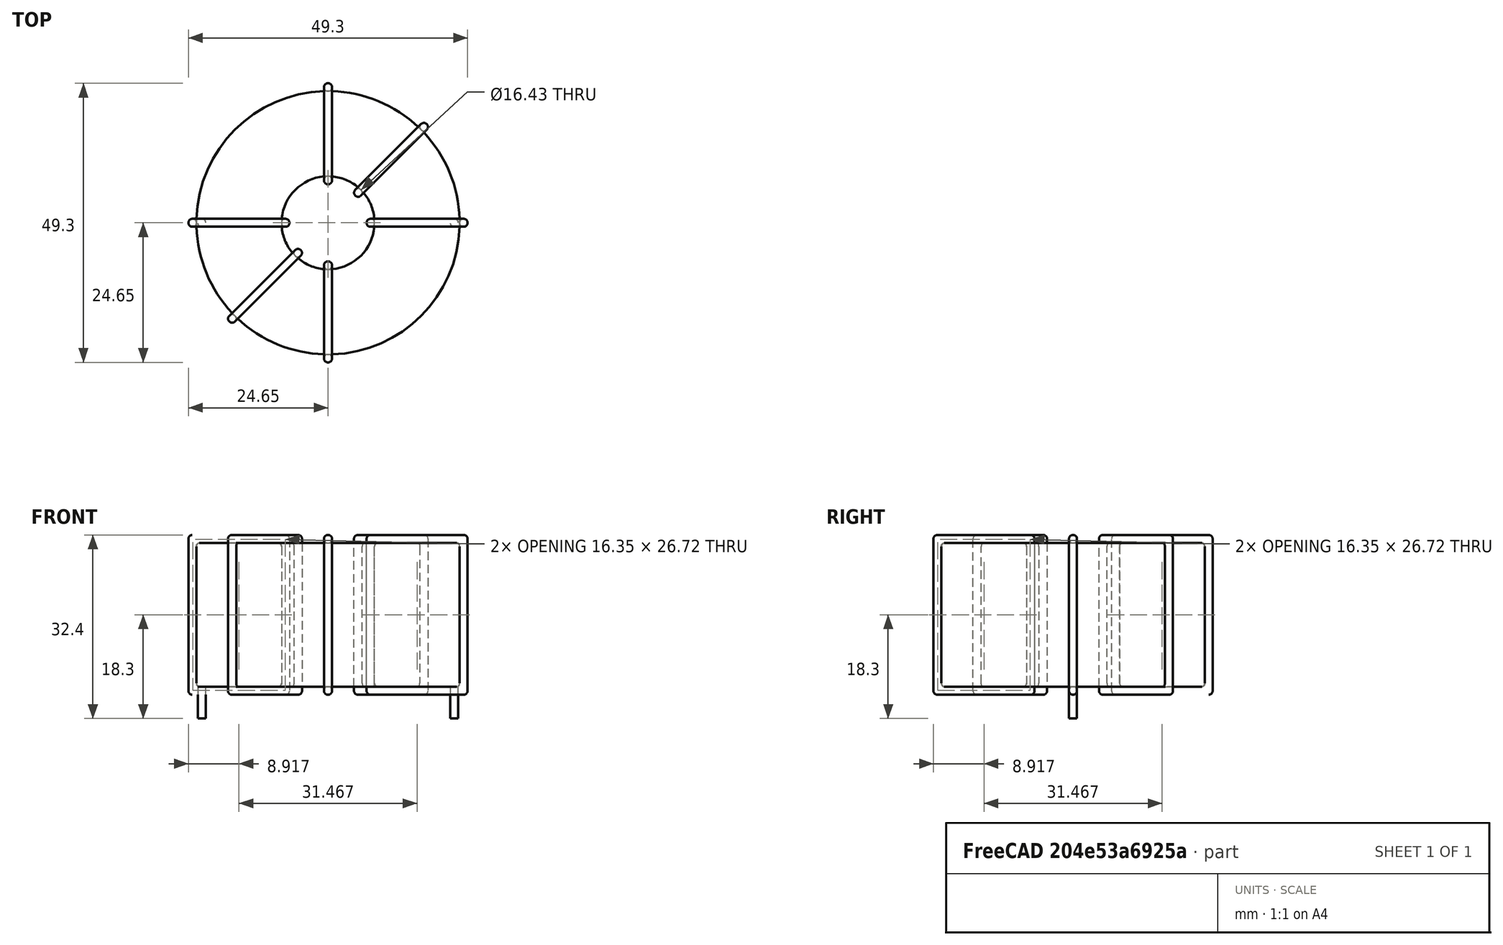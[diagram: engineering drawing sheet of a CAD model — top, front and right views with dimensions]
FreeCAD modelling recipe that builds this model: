
FCSTD DOCUMENT  (FreeCAD 0.16R6703 (Git))
Label: L_Toroid_Horizontal_D49.3mm_P44.60mm_Vishay_TJ8
License: All rights reserved
LicenseURL: http://en.wikipedia.org/wiki/All_rights_reserved
objects: Sketcher::SketchObject×6, PartDesign::Pad×6, PartDesign::Fillet×5, Spreadsheet::Sheet×1
note: 23 computed .brp shape members not serialized (recipe doc carries the construction recipe); baked Part::Feature solids carry a one-line shape summary decoded from their .brp

FEATURE [Spreadsheet::Sheet] Spreadsheet  label="dimensions"
  cells = A1=Wx; B1(Wx)=49.3; C1(WW)=16.43333333333333; D1=49.3; A2=Wy; B2(Wy)=49.3; D2=49.3; A3=RM; B3(RMx)=44.6; C3(RMy)=0; A4=d_wire; B4(d_wire)=1.4; A5=H; B5(H)=25.4; A6=offsetx; B6(offsetx)=2.349999999999998
FEATURE [Sketcher::SketchObject] Sketch
  Placement = pos=(0,0,1.9) rot=(0,0,1;0rad)
  expr: Placement.Base.z = 0.5 + Spreadsheet.d_wire
  expr: Constraints[0] = Spreadsheet.Wx / 2 - Spreadsheet.d_wire
  expr: Constraints[4] = Spreadsheet.WW / 2
  expr: Constraints[2] = Spreadsheet.RMy / 2
  expr: Constraints[1] = Spreadsheet.RMx / 2
  sketch-geometry (2):
    g0: Circle CenterX=22.3 CenterY=0 CenterZ=0 NormalX=0 NormalY=0 NormalZ=1 Radius=23.25
    g1: Circle CenterX=22.3 CenterY=0 CenterZ=0 NormalX=0 NormalY=0 NormalZ=1 Radius=8.21667
  constraints (5):
    c: Radius(g0) = 23.25
    c: DistanceX(g-1,g0) = 22.3
    c: DistanceY(g-1,g0) = 0
    c: Coincident(g1,g0)
    c: Radius(g1) = 8.21667
FEATURE [PartDesign::Pad] Pad
  Length = 25.4
  Length2 = 100
  Placement = pos=(0,0,1.9) rot=(0,0,1;0rad)
  Sketch = -> Sketch
  Type = 0
  expr: Length = Spreadsheet.H
FEATURE [Sketcher::SketchObject] Sketch001
  Placement = pos=(0,0,1.2) rot=(0,0,1;0rad)
  expr: Placement.Base.z = 0.5 + Spreadsheet.d_wire * 0.5
  expr: Constraints[4] = Spreadsheet.RMx
  expr: Constraints[2] = Spreadsheet.RMy
  expr: Constraints[1] = Spreadsheet.d_wire / 2
  sketch-geometry (2):
    g0: Circle CenterX=0 CenterY=0 CenterZ=0 NormalX=0 NormalY=0 NormalZ=1 Radius=0.7
    g1: Circle CenterX=44.6 CenterY=0 CenterZ=0 NormalX=0 NormalY=0 NormalZ=1 Radius=0.7
  constraints (5):
    c: Equal(g0,g1)
    c: Radius(g0) = 0.7
    c: DistanceY(g-1,g1) = 0
    c: Coincident(g0,g-1)
    c: DistanceX(g-1,g1) = 44.6
FEATURE [PartDesign::Pad] Pad001
  Length = 0.7
  Length2 = 4.9
  Placement = pos=(0,0,1.2) rot=(0,0,1;0rad)
  Reversed = true
  Sketch = -> Sketch001
  Type = 4
  expr: Length2 = 3.5 + Spreadsheet.d_wire
  expr: Length = Spreadsheet.d_wire / 2
FEATURE [PartDesign::Fillet] Fillet
  Base = -> Pad [Edge6,Edge3,Edge2]
  Placement = pos=(0,0,1.9) rot=(0,0,1;0rad)
  Radius = 0.5
FEATURE [Sketcher::SketchObject] Sketch003
  Placement = pos=(22.3,0,0) rot=(1,0,0;1.5708rad)
  expr: Placement.Base.x = Spreadsheet.RMx / 2
  expr: Constraints[49] = Spreadsheet.Wx - Spreadsheet.d_wire * 2
  expr: Constraints[44] = Spreadsheet.d_wire
  expr: Constraints[23] = Spreadsheet.H
  expr: Constraints[22] = Spreadsheet.Wx / 2 - Spreadsheet.d_wire
  expr: Placement.Base.y = Spreadsheet.RMy / 2
  expr: Constraints[21] = (Spreadsheet.Wx - Spreadsheet.WW) / 2 - Spreadsheet.d_wire
  expr: Constraints[19] = Spreadsheet.d_wire
  expr: Constraints[17] = Spreadsheet.d_wire
  expr: Constraints[18] = Spreadsheet.d_wire
  expr: Constraints[16] = Spreadsheet.d_wire
  sketch-geometry (16):
    g0: LineSegment StartX=-6.81667 StartY=0.5 StartZ=0 EndX=-24.65 EndY=0.5 EndZ=0
    g1: LineSegment StartX=-24.65 StartY=0.5 StartZ=0 EndX=-24.65 EndY=28.7 EndZ=0
    g2: LineSegment StartX=-24.65 StartY=28.7 StartZ=0 EndX=-6.81667 EndY=28.7 EndZ=0
    g3: LineSegment StartX=-6.81667 StartY=28.7 StartZ=0 EndX=-6.81667 EndY=0.5 EndZ=0
    g4: LineSegment StartX=-23.25 StartY=27.3 StartZ=0 EndX=-8.21667 EndY=27.3 EndZ=0
    g5: LineSegment StartX=-8.21667 StartY=27.3 StartZ=0 EndX=-8.21667 EndY=1.9 EndZ=0
    g6: LineSegment StartX=-8.21667 StartY=1.9 StartZ=0 EndX=-23.25 EndY=1.9 EndZ=0
    g7: LineSegment StartX=-23.25 StartY=1.9 StartZ=0 EndX=-23.25 EndY=27.3 EndZ=0
    g8: LineSegment StartX=6.81667 StartY=28.7 StartZ=0 EndX=24.65 EndY=28.7 EndZ=0
    g9: LineSegment StartX=24.65 StartY=28.7 StartZ=0 EndX=24.65 EndY=0.5 EndZ=0
    g10: LineSegment StartX=24.65 StartY=0.5 StartZ=0 EndX=6.81667 EndY=0.5 EndZ=0
    g11: LineSegment StartX=6.81667 StartY=0.5 StartZ=0 EndX=6.81667 EndY=28.7 EndZ=0
    g12: LineSegment StartX=8.21667 StartY=27.3 StartZ=0 EndX=23.25 EndY=27.3 EndZ=0
    g13: LineSegment StartX=23.25 StartY=27.3 StartZ=0 EndX=23.25 EndY=1.9 EndZ=0
    g14: LineSegment StartX=23.25 StartY=1.9 StartZ=0 EndX=8.21667 EndY=1.9 EndZ=0
    g15: LineSegment StartX=8.21667 StartY=1.9 StartZ=0 EndX=8.21667 EndY=27.3 EndZ=0
  constraints (50):
    c: Horizontal(g0)
    c: Coincident(g1,g0)
    c: Vertical(g1)
    c: Coincident(g2,g1)
    c: Horizontal(g2)
    c: Coincident(g3,g2)
    c: Coincident(g3,g0)
    c: Vertical(g3)
    c: Coincident(g4,g5)
    c: Coincident(g5,g6)
    c: Coincident(g6,g7)
    c: Coincident(g7,g4)
    c: Horizontal(g4)
    c: Horizontal(g6)
    c: Vertical(g5)
    c: Vertical(g7)
    c: DistanceX(g1,g4) = 1.4
    c: DistanceY(g4,g1) = 1.4
    c: DistanceX(g5,g0) = 1.4
    c: DistanceY(g0,g5) = 1.4
    c: DistanceY(g-1,g0) = 0.5
    c: DistanceX(g6,g6) = 15.0333
    c: DistanceX(g6,g-1) = 23.25
    c: DistanceY(g7,g7) = 25.4
    c: Coincident(g8,g9)
    c: Coincident(g9,g10)
    c: Coincident(g10,g11)
    c: Coincident(g11,g8)
    c: Horizontal(g8)
    c: Horizontal(g10)
    c: Vertical(g9)
    c: Vertical(g11)
    c: Coincident(g12,g13)
    c: Coincident(g13,g14)
    c: Coincident(g14,g15)
    c: Coincident(g15,g12)
    c: Horizontal(g12)
    c: Horizontal(g14)
    c: Vertical(g13)
    c: Vertical(g15)
    c: DistanceY(g8,g2) = 0
    c: DistanceY(g10,g0) = 0
    c: DistanceY(g14,g5) = 0
    c: DistanceY(g12,g4) = 0
    c: DistanceX(g8,g12) = 1.4
    c: Equal(g8,g2)
    c: Equal(g12,g4)
    c: Equal(g9,g1)
    c: Equal(g13,g7)
    c: DistanceX(g4,g12) = 46.5
FEATURE [PartDesign::Pad] Pad002
  Length = 1.4
  Length2 = 100
  Midplane = true
  Placement = pos=(22.3,0,0) rot=(1,0,0;1.5708rad)
  Sketch = -> Sketch003
  Type = 0
  expr: Length = Spreadsheet.d_wire
FEATURE [PartDesign::Fillet] Fillet001
  Base = -> Pad002 [Edge38,Edge41,Edge42,Edge43,Edge29,Edge32,Edge33,Edge34,Edge25,Edge35,Edge36,Edge13,Edge14,Edge15,Edge16,Edge17,Edge18,Edge19,Edge1,Edge2,Edge3,Edge4,Edge5,Edge6,Edge7,Edge37,Edge39,Edge40,Edge20,Edge23,Edge24,Edge21,Edge22,Edge8,Edge9,Edge10,Edge11,Edge12,Edge26,Edge27,+8 more]
  Placement = pos=(22.3,0,0) rot=(1,0,0;1.5708rad)
  Radius = 0.658
  expr: Radius = Spreadsheet.d_wire * 0.47
FEATURE [Sketcher::SketchObject] Sketch004
  Placement = pos=(22.3,0,0) rot=(0.862856,0.357407,0.357407;1.71777rad)
  expr: Placement.Base.x = Spreadsheet.RMx / 2
  expr: Constraints[49] = Spreadsheet.Wx - 2 * Spreadsheet.d_wire
  expr: Constraints[44] = Spreadsheet.d_wire
  expr: Constraints[23] = Spreadsheet.H
  expr: Constraints[22] = Spreadsheet.Wx / 2 - Spreadsheet.d_wire
  expr: Placement.Base.y = Spreadsheet.RMy / 2
  expr: Constraints[21] = (Spreadsheet.Wx - Spreadsheet.WW) / 2 - Spreadsheet.d_wire
  expr: Constraints[19] = Spreadsheet.d_wire
  expr: Constraints[17] = Spreadsheet.d_wire
  expr: Constraints[18] = Spreadsheet.d_wire
  expr: Constraints[16] = Spreadsheet.d_wire
  sketch-geometry (16):
    g0: LineSegment StartX=-6.81667 StartY=0.5 StartZ=0 EndX=-24.65 EndY=0.5 EndZ=0
    g1: LineSegment StartX=-24.65 StartY=0.5 StartZ=0 EndX=-24.65 EndY=28.7 EndZ=0
    g2: LineSegment StartX=-24.65 StartY=28.7 StartZ=0 EndX=-6.81667 EndY=28.7 EndZ=0
    g3: LineSegment StartX=-6.81667 StartY=28.7 StartZ=0 EndX=-6.81667 EndY=0.5 EndZ=0
    g4: LineSegment StartX=-23.25 StartY=27.3 StartZ=0 EndX=-8.21667 EndY=27.3 EndZ=0
    g5: LineSegment StartX=-8.21667 StartY=27.3 StartZ=0 EndX=-8.21667 EndY=1.9 EndZ=0
    g6: LineSegment StartX=-8.21667 StartY=1.9 StartZ=0 EndX=-23.25 EndY=1.9 EndZ=0
    g7: LineSegment StartX=-23.25 StartY=1.9 StartZ=0 EndX=-23.25 EndY=27.3 EndZ=0
    g8: LineSegment StartX=6.81667 StartY=28.7 StartZ=0 EndX=24.65 EndY=28.7 EndZ=0
    g9: LineSegment StartX=24.65 StartY=28.7 StartZ=0 EndX=24.65 EndY=0.5 EndZ=0
    g10: LineSegment StartX=24.65 StartY=0.5 StartZ=0 EndX=6.81667 EndY=0.5 EndZ=0
    g11: LineSegment StartX=6.81667 StartY=0.5 StartZ=0 EndX=6.81667 EndY=28.7 EndZ=0
    g12: LineSegment StartX=8.21667 StartY=27.3 StartZ=0 EndX=23.25 EndY=27.3 EndZ=0
    g13: LineSegment StartX=23.25 StartY=27.3 StartZ=0 EndX=23.25 EndY=1.9 EndZ=0
    g14: LineSegment StartX=23.25 StartY=1.9 StartZ=0 EndX=8.21667 EndY=1.9 EndZ=0
    g15: LineSegment StartX=8.21667 StartY=1.9 StartZ=0 EndX=8.21667 EndY=27.3 EndZ=0
  constraints (50):
    c: Horizontal(g0)
    c: Coincident(g1,g0)
    c: Vertical(g1)
    c: Coincident(g2,g1)
    c: Horizontal(g2)
    c: Coincident(g3,g2)
    c: Coincident(g3,g0)
    c: Vertical(g3)
    c: Coincident(g4,g5)
    c: Coincident(g5,g6)
    c: Coincident(g6,g7)
    c: Coincident(g7,g4)
    c: Horizontal(g4)
    c: Horizontal(g6)
    c: Vertical(g5)
    c: Vertical(g7)
    c: DistanceX(g1,g4) = 1.4
    c: DistanceY(g4,g1) = 1.4
    c: DistanceX(g5,g0) = 1.4
    c: DistanceY(g0,g5) = 1.4
    c: DistanceY(g-1,g0) = 0.5
    c: DistanceX(g6,g6) = 15.0333
    c: DistanceX(g6,g-1) = 23.25
    c: DistanceY(g7,g7) = 25.4
    c: Coincident(g8,g9)
    c: Coincident(g9,g10)
    c: Coincident(g10,g11)
    c: Coincident(g11,g8)
    c: Horizontal(g8)
    c: Horizontal(g10)
    c: Vertical(g9)
    c: Vertical(g11)
    c: Coincident(g12,g13)
    c: Coincident(g13,g14)
    c: Coincident(g14,g15)
    c: Coincident(g15,g12)
    c: Horizontal(g12)
    c: Horizontal(g14)
    c: Vertical(g13)
    c: Vertical(g15)
    c: DistanceY(g8,g2) = 0
    c: DistanceY(g10,g0) = 0
    c: DistanceY(g14,g5) = 0
    c: DistanceY(g12,g4) = 0
    c: DistanceX(g8,g12) = 1.4
    c: Equal(g8,g2)
    c: Equal(g12,g4)
    c: Equal(g9,g1)
    c: Equal(g13,g7)
    c: DistanceX(g4,g12) = 46.5
FEATURE [PartDesign::Pad] Pad003
  Length = 1.4
  Length2 = 100
  Midplane = true
  Placement = pos=(22.3,0,0) rot=(0.862856,0.357407,0.357407;1.71777rad)
  Sketch = -> Sketch004
  Type = 0
  expr: Length = Spreadsheet.d_wire
FEATURE [PartDesign::Fillet] Fillet002
  Base = -> Pad003 [Edge38,Edge41,Edge42,Edge43,Edge29,Edge32,Edge33,Edge34,Edge25,Edge35,Edge36,Edge13,Edge14,Edge15,Edge16,Edge17,Edge18,Edge19,Edge1,Edge2,Edge3,Edge4,Edge5,Edge6,Edge7,Edge37,Edge39,Edge40,Edge20,Edge23,Edge24,Edge21,Edge22,Edge8,Edge9,Edge10,Edge11,Edge12,Edge26,Edge27,+8 more]
  Placement = pos=(22.3,0,0) rot=(0.862856,0.357407,0.357407;1.71777rad)
  Radius = 0.658
  expr: Radius = Spreadsheet.d_wire * 0.47
FEATURE [Sketcher::SketchObject] Sketch005
  Placement = pos=(22.3,0,0) rot=(0.862856,-0.357407,-0.357407;1.71777rad)
  expr: Placement.Base.x = Spreadsheet.RMx / 2
  expr: Constraints[49] = Spreadsheet.Wx - 2 * Spreadsheet.d_wire
  expr: Constraints[44] = Spreadsheet.d_wire
  expr: Constraints[23] = Spreadsheet.H
  expr: Constraints[22] = Spreadsheet.Wx / 2 - Spreadsheet.d_wire
  expr: Placement.Base.y = Spreadsheet.RMy / 2
  expr: Constraints[21] = (Spreadsheet.Wx - Spreadsheet.WW) / 2 - Spreadsheet.d_wire
  expr: Constraints[19] = Spreadsheet.d_wire
  expr: Constraints[17] = Spreadsheet.d_wire
  expr: Constraints[18] = Spreadsheet.d_wire
  expr: Constraints[16] = Spreadsheet.d_wire
  sketch-geometry (16):
    g0: LineSegment StartX=-6.81667 StartY=0.5 StartZ=0 EndX=-24.65 EndY=0.5 EndZ=0
    g1: LineSegment StartX=-24.65 StartY=0.5 StartZ=0 EndX=-24.65 EndY=28.7 EndZ=0
    g2: LineSegment StartX=-24.65 StartY=28.7 StartZ=0 EndX=-6.81667 EndY=28.7 EndZ=0
    g3: LineSegment StartX=-6.81667 StartY=28.7 StartZ=0 EndX=-6.81667 EndY=0.5 EndZ=0
    g4: LineSegment StartX=-23.25 StartY=27.3 StartZ=0 EndX=-8.21667 EndY=27.3 EndZ=0
    g5: LineSegment StartX=-8.21667 StartY=27.3 StartZ=0 EndX=-8.21667 EndY=1.9 EndZ=0
    g6: LineSegment StartX=-8.21667 StartY=1.9 StartZ=0 EndX=-23.25 EndY=1.9 EndZ=0
    g7: LineSegment StartX=-23.25 StartY=1.9 StartZ=0 EndX=-23.25 EndY=27.3 EndZ=0
    g8: LineSegment StartX=6.81667 StartY=28.7 StartZ=0 EndX=24.65 EndY=28.7 EndZ=0
    g9: LineSegment StartX=24.65 StartY=28.7 StartZ=0 EndX=24.65 EndY=0.5 EndZ=0
    g10: LineSegment StartX=24.65 StartY=0.5 StartZ=0 EndX=6.81667 EndY=0.5 EndZ=0
    g11: LineSegment StartX=6.81667 StartY=0.5 StartZ=0 EndX=6.81667 EndY=28.7 EndZ=0
    g12: LineSegment StartX=8.21667 StartY=27.3 StartZ=0 EndX=23.25 EndY=27.3 EndZ=0
    g13: LineSegment StartX=23.25 StartY=27.3 StartZ=0 EndX=23.25 EndY=1.9 EndZ=0
    g14: LineSegment StartX=23.25 StartY=1.9 StartZ=0 EndX=8.21667 EndY=1.9 EndZ=0
    g15: LineSegment StartX=8.21667 StartY=1.9 StartZ=0 EndX=8.21667 EndY=27.3 EndZ=0
  constraints (50):
    c: Horizontal(g0)
    c: Coincident(g1,g0)
    c: Vertical(g1)
    c: Coincident(g2,g1)
    c: Horizontal(g2)
    c: Coincident(g3,g2)
    c: Coincident(g3,g0)
    c: Vertical(g3)
    c: Coincident(g4,g5)
    c: Coincident(g5,g6)
    c: Coincident(g6,g7)
    c: Coincident(g7,g4)
    c: Horizontal(g4)
    c: Horizontal(g6)
    c: Vertical(g5)
    c: Vertical(g7)
    c: DistanceX(g1,g4) = 1.4
    c: DistanceY(g4,g1) = 1.4
    c: DistanceX(g5,g0) = 1.4
    c: DistanceY(g0,g5) = 1.4
    c: DistanceY(g-1,g0) = 0.5
    c: DistanceX(g6,g6) = 15.0333
    c: DistanceX(g6,g-1) = 23.25
    c: DistanceY(g7,g7) = 25.4
    c: Coincident(g8,g9)
    c: Coincident(g9,g10)
    c: Coincident(g10,g11)
    c: Coincident(g11,g8)
    c: Horizontal(g8)
    c: Horizontal(g10)
    c: Vertical(g9)
    c: Vertical(g11)
    c: Coincident(g12,g13)
    c: Coincident(g13,g14)
    c: Coincident(g14,g15)
    c: Coincident(g15,g12)
    c: Horizontal(g12)
    c: Horizontal(g14)
    c: Vertical(g13)
    c: Vertical(g15)
    c: DistanceY(g8,g2) = 0
    c: DistanceY(g10,g0) = 0
    c: DistanceY(g14,g5) = 0
    c: DistanceY(g12,g4) = 0
    c: DistanceX(g8,g12) = 1.4
    c: Equal(g8,g2)
    c: Equal(g12,g4)
    c: Equal(g9,g1)
    c: Equal(g13,g7)
    c: DistanceX(g4,g12) = 46.5
FEATURE [PartDesign::Pad] Pad004
  Length = 1.4
  Length2 = 100
  Midplane = true
  Placement = pos=(22.3,0,0) rot=(0.862856,-0.357407,-0.357407;1.71777rad)
  Sketch = -> Sketch005
  Type = 0
  expr: Length = Spreadsheet.d_wire
FEATURE [PartDesign::Fillet] Fillet003
  Base = -> Pad004 [Edge38,Edge41,Edge42,Edge43,Edge29,Edge32,Edge33,Edge34,Edge25,Edge35,Edge36,Edge13,Edge14,Edge15,Edge16,Edge17,Edge18,Edge19,Edge1,Edge2,Edge3,Edge4,Edge5,Edge6,Edge7,Edge37,Edge39,Edge40,Edge20,Edge23,Edge24,Edge21,Edge22,Edge8,Edge9,Edge10,Edge11,Edge12,Edge26,Edge27,+8 more]
  Placement = pos=(22.3,0,0) rot=(0.862856,-0.357407,-0.357407;1.71777rad)
  Radius = 0.658
  expr: Radius = Spreadsheet.d_wire * 0.47
FEATURE [Sketcher::SketchObject] Sketch006
  Placement = pos=(22.3,0,0) rot=(0.57735,0.57735,0.57735;2.0944rad)
  expr: Placement.Base.x = Spreadsheet.RMx / 2
  expr: Constraints[49] = Spreadsheet.Wx - Spreadsheet.d_wire * 2
  expr: Constraints[44] = Spreadsheet.d_wire
  expr: Constraints[23] = Spreadsheet.H
  expr: Constraints[22] = Spreadsheet.Wx / 2 - Spreadsheet.d_wire
  expr: Placement.Base.y = Spreadsheet.RMy / 2
  expr: Constraints[21] = (Spreadsheet.Wx - Spreadsheet.WW) / 2 - Spreadsheet.d_wire
  expr: Constraints[19] = Spreadsheet.d_wire
  expr: Constraints[17] = Spreadsheet.d_wire
  expr: Constraints[18] = Spreadsheet.d_wire
  expr: Constraints[16] = Spreadsheet.d_wire
  sketch-geometry (16):
    g0: LineSegment StartX=-6.81667 StartY=0.5 StartZ=0 EndX=-24.65 EndY=0.5 EndZ=0
    g1: LineSegment StartX=-24.65 StartY=0.5 StartZ=0 EndX=-24.65 EndY=28.7 EndZ=0
    g2: LineSegment StartX=-24.65 StartY=28.7 StartZ=0 EndX=-6.81667 EndY=28.7 EndZ=0
    g3: LineSegment StartX=-6.81667 StartY=28.7 StartZ=0 EndX=-6.81667 EndY=0.5 EndZ=0
    g4: LineSegment StartX=-23.25 StartY=27.3 StartZ=0 EndX=-8.21667 EndY=27.3 EndZ=0
    g5: LineSegment StartX=-8.21667 StartY=27.3 StartZ=0 EndX=-8.21667 EndY=1.9 EndZ=0
    g6: LineSegment StartX=-8.21667 StartY=1.9 StartZ=0 EndX=-23.25 EndY=1.9 EndZ=0
    g7: LineSegment StartX=-23.25 StartY=1.9 StartZ=0 EndX=-23.25 EndY=27.3 EndZ=0
    g8: LineSegment StartX=6.81667 StartY=28.7 StartZ=0 EndX=24.65 EndY=28.7 EndZ=0
    g9: LineSegment StartX=24.65 StartY=28.7 StartZ=0 EndX=24.65 EndY=0.5 EndZ=0
    g10: LineSegment StartX=24.65 StartY=0.5 StartZ=0 EndX=6.81667 EndY=0.5 EndZ=0
    g11: LineSegment StartX=6.81667 StartY=0.5 StartZ=0 EndX=6.81667 EndY=28.7 EndZ=0
    g12: LineSegment StartX=8.21667 StartY=27.3 StartZ=0 EndX=23.25 EndY=27.3 EndZ=0
    g13: LineSegment StartX=23.25 StartY=27.3 StartZ=0 EndX=23.25 EndY=1.9 EndZ=0
    g14: LineSegment StartX=23.25 StartY=1.9 StartZ=0 EndX=8.21667 EndY=1.9 EndZ=0
    g15: LineSegment StartX=8.21667 StartY=1.9 StartZ=0 EndX=8.21667 EndY=27.3 EndZ=0
  constraints (50):
    c: Horizontal(g0)
    c: Coincident(g1,g0)
    c: Vertical(g1)
    c: Coincident(g2,g1)
    c: Horizontal(g2)
    c: Coincident(g3,g2)
    c: Coincident(g3,g0)
    c: Vertical(g3)
    c: Coincident(g4,g5)
    c: Coincident(g5,g6)
    c: Coincident(g6,g7)
    c: Coincident(g7,g4)
    c: Horizontal(g4)
    c: Horizontal(g6)
    c: Vertical(g5)
    c: Vertical(g7)
    c: DistanceX(g1,g4) = 1.4
    c: DistanceY(g4,g1) = 1.4
    c: DistanceX(g5,g0) = 1.4
    c: DistanceY(g0,g5) = 1.4
    c: DistanceY(g-1,g0) = 0.5
    c: DistanceX(g6,g6) = 15.0333
    c: DistanceX(g6,g-1) = 23.25
    c: DistanceY(g7,g7) = 25.4
    c: Coincident(g8,g9)
    c: Coincident(g9,g10)
    c: Coincident(g10,g11)
    c: Coincident(g11,g8)
    c: Horizontal(g8)
    c: Horizontal(g10)
    c: Vertical(g9)
    c: Vertical(g11)
    c: Coincident(g12,g13)
    c: Coincident(g13,g14)
    c: Coincident(g14,g15)
    c: Coincident(g15,g12)
    c: Horizontal(g12)
    c: Horizontal(g14)
    c: Vertical(g13)
    c: Vertical(g15)
    c: DistanceY(g8,g2) = 0
    c: DistanceY(g10,g0) = 0
    c: DistanceY(g14,g5) = 0
    c: DistanceY(g12,g4) = 0
    c: DistanceX(g8,g12) = 1.4
    c: Equal(g8,g2)
    c: Equal(g12,g4)
    c: Equal(g9,g1)
    c: Equal(g13,g7)
    c: DistanceX(g4,g12) = 46.5
FEATURE [PartDesign::Pad] Pad005
  Length = 1.4
  Length2 = 100
  Midplane = true
  Placement = pos=(22.3,0,0) rot=(0.57735,0.57735,0.57735;2.0944rad)
  Sketch = -> Sketch006
  Type = 0
  expr: Length = Spreadsheet.d_wire
FEATURE [PartDesign::Fillet] Fillet004
  Base = -> Pad005 [Edge38,Edge41,Edge42,Edge43,Edge29,Edge32,Edge33,Edge34,Edge25,Edge35,Edge36,Edge13,Edge14,Edge15,Edge16,Edge17,Edge18,Edge19,Edge1,Edge2,Edge3,Edge4,Edge5,Edge6,Edge7,Edge37,Edge39,Edge40,Edge20,Edge23,Edge24,Edge21,Edge22,Edge8,Edge9,Edge10,Edge11,Edge12,Edge26,Edge27,+8 more]
  Placement = pos=(22.3,0,0) rot=(0.57735,0.57735,0.57735;2.0944rad)
  Radius = 0.658
  expr: Radius = Spreadsheet.d_wire * 0.47
